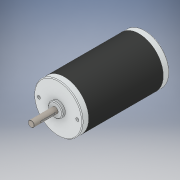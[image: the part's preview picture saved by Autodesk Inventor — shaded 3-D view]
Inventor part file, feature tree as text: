
AUTODESK INVENTOR PART (.ipt)
format: ipt  version: 2018 (Build 220112000, 112)  size: 173,056 bytes
history: native  units: in
note: dims shown in document units (in); Inventor stores cm internally (conversion verified against a paired STEP export)
features: fillet x1
ambient origin geometry x8: Origin, YZ Plane, XZ Plane, XY Plane, X Axis, Y Axis, Z Axis, Center Point
bodies: Solid1 (feature_tree)
feature tree (1):
  fillet  "Fillet5"  [1 undecoded]
note: 1 required parameter value undecoded (feature->parameter linkage not recoverable at this tier; creation-order binding heuristic only, values carry confidence <= 0.55)
